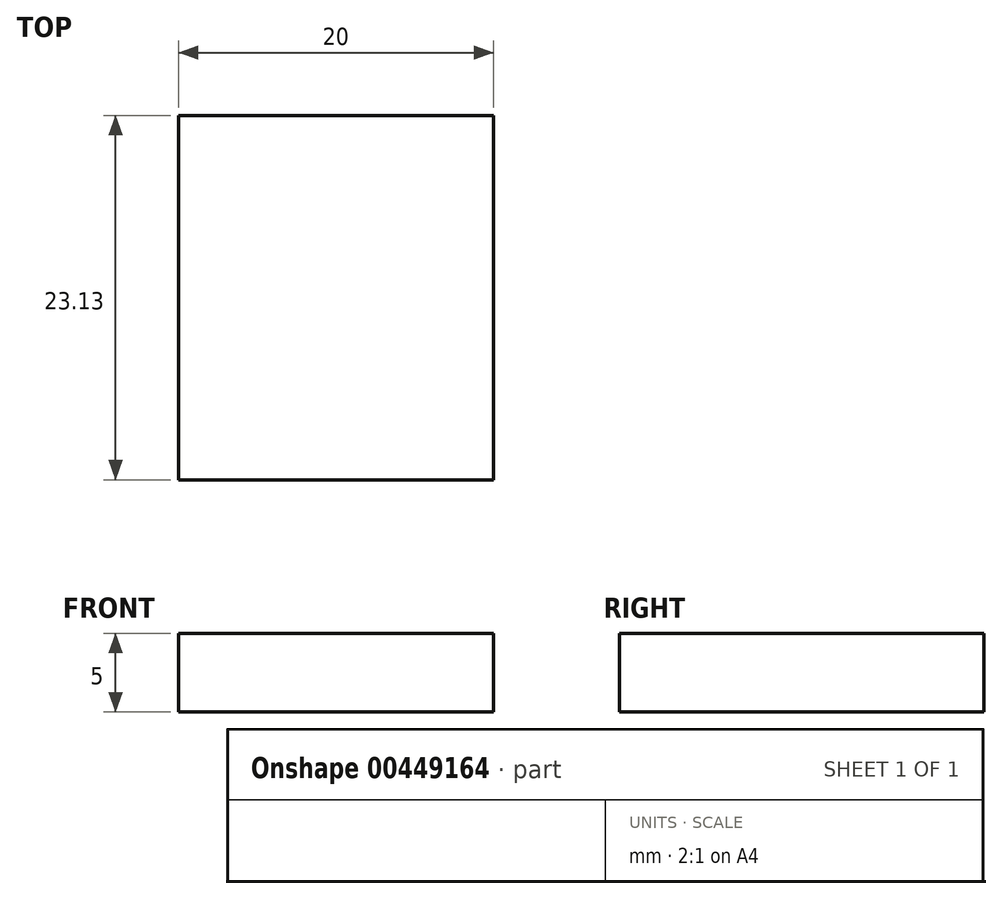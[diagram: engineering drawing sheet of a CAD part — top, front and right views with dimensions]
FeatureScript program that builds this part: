
annotation { "Feature Type Name" : "Feature", "Feature Type Description" : "" }
export const myFeature = defineFeature(function(context is Context, id is Id, definition is map)
    precondition{}
    {
        {
            var Q0;
            Q0=qCreatedBy(makeId("Top.planeOp"),FACE);
            var sketch = newSketch(context, id + "F0", { "sketchPlane" : qUnion([Q0])});
            skLineSegment(sketch, "E0.bottom", {"start": v(0, 0) * mm, "end": v(20, 0) * mm});
            skLineSegment(sketch, "E0.top", {"start": v(0, 23.13) * mm, "end": v(20, 23.13) * mm});
            skLineSegment(sketch, "E0.left", {"start": v(0, 0) * mm, "end": v(0, 23.13) * mm});
            skLineSegment(sketch, "E0.right", {"start": v(20, 0) * mm, "end": v(20, 23.13) * mm});
            skSolve(sketch);
        }
        {
            var Q0;
            Q0=makeQuery(id+"F0.imprint","IMPRINT",FACE,{"disambiguationData":[TD([[makeQuery(id+"F0.imprint","IMPRINT",EDGE,{"derivedFrom":sQuery(id+"F0.wireOp",EDGE,"E0.bottom")}),1.0]])]});
            extrude(context, id + "F1", {"entities" : qUnion([Q0]), "depth" : 5 * mm});
        }
    });
